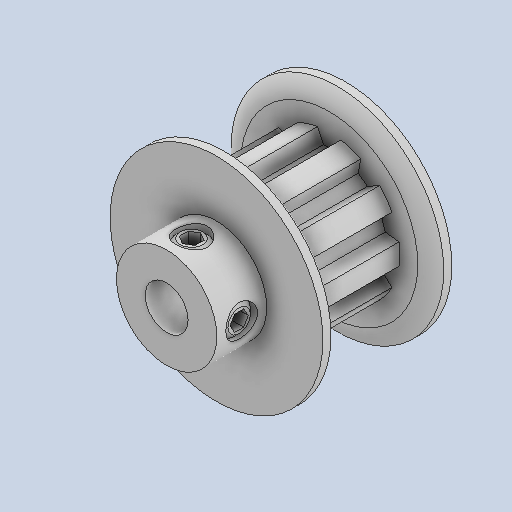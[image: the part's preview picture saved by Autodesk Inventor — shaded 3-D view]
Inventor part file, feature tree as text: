
AUTODESK INVENTOR PART (.ipt)
format: ipt  version: 2023 (Build 270158000, 158)  size: 359,424 bytes
history: native  units: mm
features: sketch x1, pattern_circular x1
ambient origin geometry x8: Origin, YZ Plane, XZ Plane, XY Plane, X Axis, Y Axis, Z Axis, Center Point
bodies: Solid1 (feature_tree)
feature tree (2):
  sketch  "Sketch1"
  pattern_circular  "CirPattern2"
